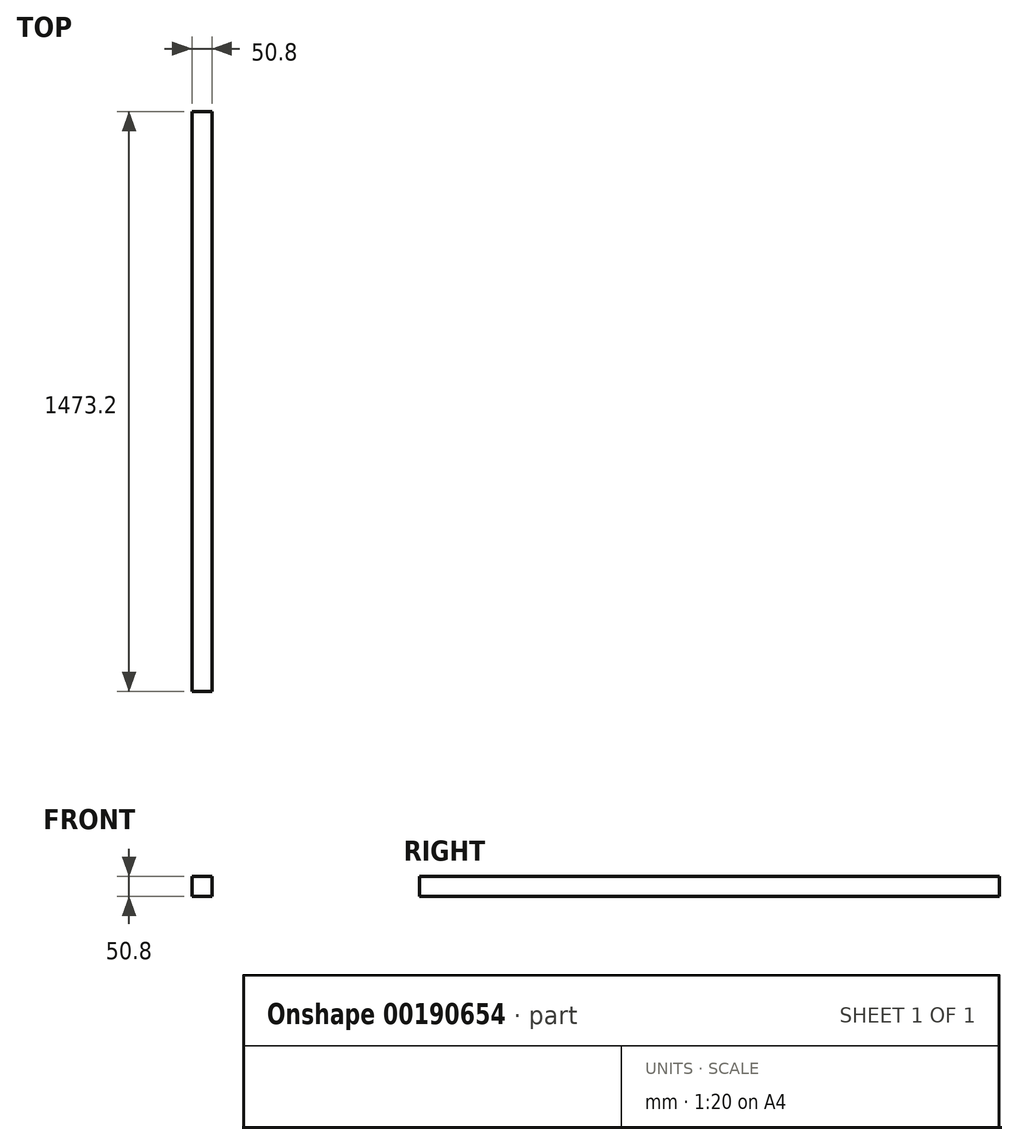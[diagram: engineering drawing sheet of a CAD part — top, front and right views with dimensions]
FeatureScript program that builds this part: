
annotation { "Feature Type Name" : "Feature", "Feature Type Description" : "" }
export const myFeature = defineFeature(function(context is Context, id is Id, definition is map)
    precondition{}
    {
        {
            var Q0;
            Q0=qCreatedBy(makeId("Front.planeOp"),FACE);
            cPlane(context, id + "F0", {"entities" : qUnion([Q0]), "cplaneType" : CPlaneType.OFFSET, "offset" : 736.6 * mm, "width" : 152.4 * mm, "height" : 152.4 * mm});
        }
        {
            var Q0;
            Q0=qCreatedBy(id+"F0.planeOp",FACE);
            var sketch = newSketch(context, id + "F1", { "sketchPlane" : qUnion([Q0])});
            skLineSegment(sketch, "E0.bottom", {"start": v(25.4, -25.4) * mm, "end": v(-25.4, -25.4) * mm});
            skLineSegment(sketch, "E0.top", {"start": v(25.4, 25.4) * mm, "end": v(-25.4, 25.4) * mm});
            skLineSegment(sketch, "E0.left", {"start": v(25.4, -25.4) * mm, "end": v(25.4, 25.4) * mm});
            skLineSegment(sketch, "E0.right", {"start": v(-25.4, -25.4) * mm, "end": v(-25.4, 25.4) * mm});
            skPoint(sketch, "E0.middle", {"position": v(0, 0) * mm});
            skSolve(sketch);
        }
        {
            var Q0;
            Q0=makeQuery(id+"F1.imprint","IMPRINT",FACE,{"disambiguationData":[TD([[makeQuery(id+"F1.imprint","IMPRINT",EDGE,{"derivedFrom":sQuery(id+"F1.wireOp",EDGE,"E0.bottom")}),-1.0]])]});
            extrude(context, id + "F2", {"entities" : qUnion([Q0]), "oppositeDirection" : true, "depth" : 1473.2 * mm});
        }
    });
